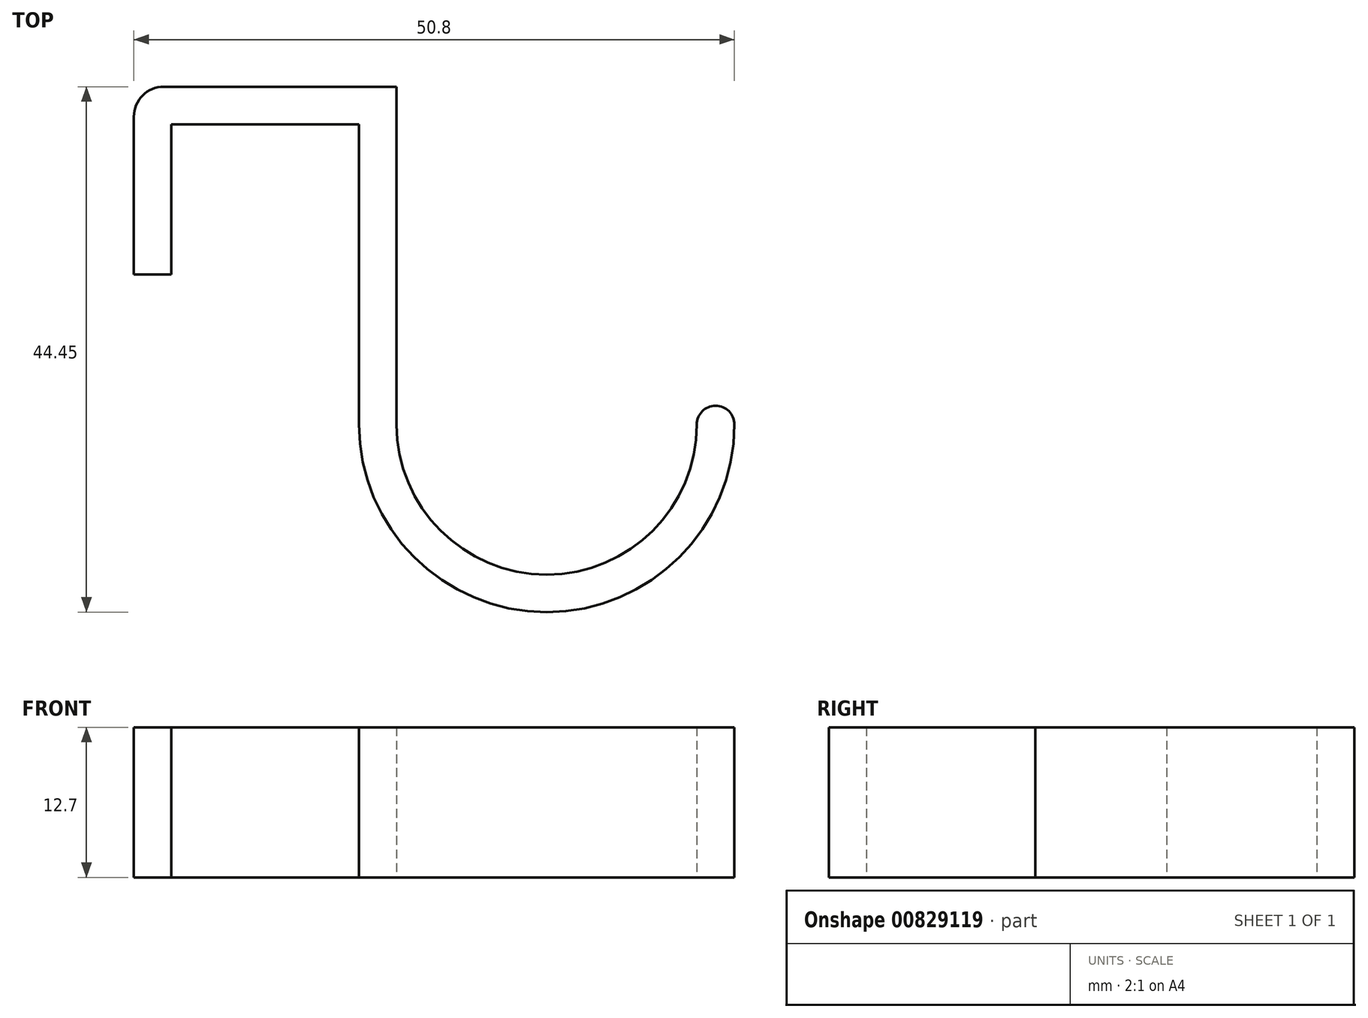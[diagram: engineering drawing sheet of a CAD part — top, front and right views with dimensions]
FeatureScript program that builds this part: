
annotation { "Feature Type Name" : "Feature", "Feature Type Description" : "" }
export const myFeature = defineFeature(function(context is Context, id is Id, definition is map)
    precondition{}
    {
        {
            var Q0;
            Q0=qCreatedBy(makeId("Top.planeOp"),FACE);
            var sketch = newSketch(context, id + "F0", { "sketchPlane" : qUnion([Q0])});
            skLineSegment(sketch, "E0", {"start": v(-7.94, -12.7) * mm, "end": v(-11.11, -12.7) * mm});
            skLineSegment(sketch, "E1", {"start": v(-11.11, -12.7) * mm, "end": v(-11.11, 3.17) * mm});
            skLineSegment(sketch, "E2", {"start": v(-11.11, 3.17) * mm, "end": v(11.11, 3.18) * mm});
            skLineSegment(sketch, "E3", {"start": v(11.11, 3.18) * mm, "end": v(11.11, -25.4) * mm});
            skLineSegment(sketch, "E4", {"start": v(11.11, -25.4) * mm, "end": v(36.51, -25.4) * mm, "construction": true});
            skLineSegment(sketch, "E5", {"start": v(-7.94, -12.7) * mm, "end": v(-7.94, 0) * mm});
            skLineSegment(sketch, "E6", {"start": v(-7.94, 0) * mm, "end": v(7.94, 0) * mm});
            skLineSegment(sketch, "E7", {"start": v(7.94, 0) * mm, "end": v(7.94, -25.4) * mm});
            skLineSegment(sketch, "E8", {"start": v(7.94, -25.4) * mm, "end": v(11.11, -25.4) * mm, "construction": true});
            skArc(sketch, "E9", {"start": v(11.11, -25.4) * mm, "mid": v(23.81, -38.1) * mm, "end": v(36.51, -25.4) * mm});
            skArc(sketch, "E10", {"start": v(7.94, -25.4) * mm, "mid": v(23.81, -41.27) * mm, "end": v(39.69, -25.4) * mm});
            skLineSegment(sketch, "E11", {"start": v(36.51, -25.4) * mm, "end": v(39.69, -25.4) * mm, "construction": true});
            skArc(sketch, "E12", {"start": v(36.51, -25.4) * mm, "mid": v(38.1, -23.81) * mm, "end": v(39.69, -25.4) * mm});
            skSolve(sketch);
        }
        {
            var Q0;
            Q0=makeQuery(id+"F0.imprint","IMPRINT",FACE,{"disambiguationData":[TD([[makeQuery(id+"F0.imprint","IMPRINT",EDGE,{"derivedFrom":sQuery(id+"F0.wireOp",EDGE,"E0")}),-1.0]])]});
            extrude(context, id + "F1", {"entities" : qUnion([Q0]), "depth" : 12.7 * mm, "offsetDistance" : 25.4 * mm});
        }
        {
            var Q0;
            Q0=makeQuery(id+"F1.opExtrude","SWEPT_EDGE",EDGE,{"disambiguationData":[OSD([sQuery(id+"F0.wireOp",EDGE,"E1"),sQuery(id+"F0.wireOp",EDGE,"E2")])]});
            fillet(context, id + "F2", {"entities" : qUnion([Q0]), "radius" : 2.54 * mm, "tangentPropagation" : true, "allowEdgeOverflow" : false});
        }
    });
